# Revit family: Diffuser-Carnes-Square_Rectangular-Neck-SEEA
name_source: partatom
category: Duct Accessories
revit_build: Autodesk Revit MEP 2014 (Build: 20130308_1515(x64)
units: mm (PartAtom-declared; Revit-internal decimal feet)

## types (24) — shared parameters
Catalog = http://www.carnes.com
Default Elevation = 0"
Description = Square and Rectangular Diffusers
Flow = 0 CFM
Manufacturer = CARNES COMPANY
Model = SEEA
Product Page URL = http://www.carnes.com
Rapid Induction Vanes = http://www.carnes.com
Revit Object Download Link = http://library.smartbim.com
Round Neck Option = http://www.carnes.com
Specification Sheet = http://www.carnes.com
Subcatagory = Air Distribution
Supply Connector = Yes
URL = http://www.carnes.com
Unit = Metal - Carnes - Aluminum

## per-type parameters (varying)
| type | A | B | Overall Length | Overall Width |
| SEEA-6Inx6In | 6" | 6" | 9" | 8 3/4" |
| SEEA-6Inx9In | 6" | 9" | 12" | 8 3/4" |
| SEEA-6Inx12In | 6" | 12" | 15" | 8 3/4" |
| SEEA-6Inx15In | 6" | 15" | 18" | 8 3/4" |
| SEEA-6Inx18In | 6" | 18" | 21" | 8 3/4" |
| SEEA-6Inx21In | 6" | 21" | 24" | 8 3/4" |
| SEEA-9Inx9In | 9" | 9" | 12" | 11 3/4" |
| SEEA-9Inx12In | 9" | 12" | 15" | 11 3/4" |
| SEEA-9Inx15In | 9" | 15" | 18" | 11 3/4" |
| SEEA-9Inx18In | 9" | 18" | 21" | 11 3/4" |
| SEEA-9Inx21In | 9" | 21" | 24" | 11 3/4" |
| SEEA-12Inx12In | 12" | 12" | 15" | 14 3/4" |
| SEEA-12Inx15In | 12" | 15" | 18" | 14 3/4" |
| SEEA-12Inx18In | 12" | 18" | 21" | 14 3/4" |
| SEEA-12Inx21In | 12" | 21" | 24" | 14 3/4" |
| SEEA-15Inx15In | 15" | 15" | 18" | 17 3/4" |
| SEEA-15Inx18In | 15" | 18" | 21" | 17 3/4" |
| SEEA-15Inx21In | 15" | 21" | 24" | 17 3/4" |
| SEEA-18Inx18In | 18" | 18" | 21" | 20 3/4" |
| SEEA-18Inx21In | 18" | 21" | 24" | 20 3/4" |
| SEEA-21Inx21In | 21" | 21" | 24" | 23 3/4" |
| SEEA-21Inx24In | 21" | 24" | 27" | 23 3/4" |
| SEEA-24Inx24In | 24" | 24" | 27" | 26 3/4" |
| SEEA-45Inx45In | 45" | 45" | 48" | 47 3/4" |

## geometry (parser evidence)
native form markers: Blend x4, Sweep x4
no freeform markers — native parametric forms only
